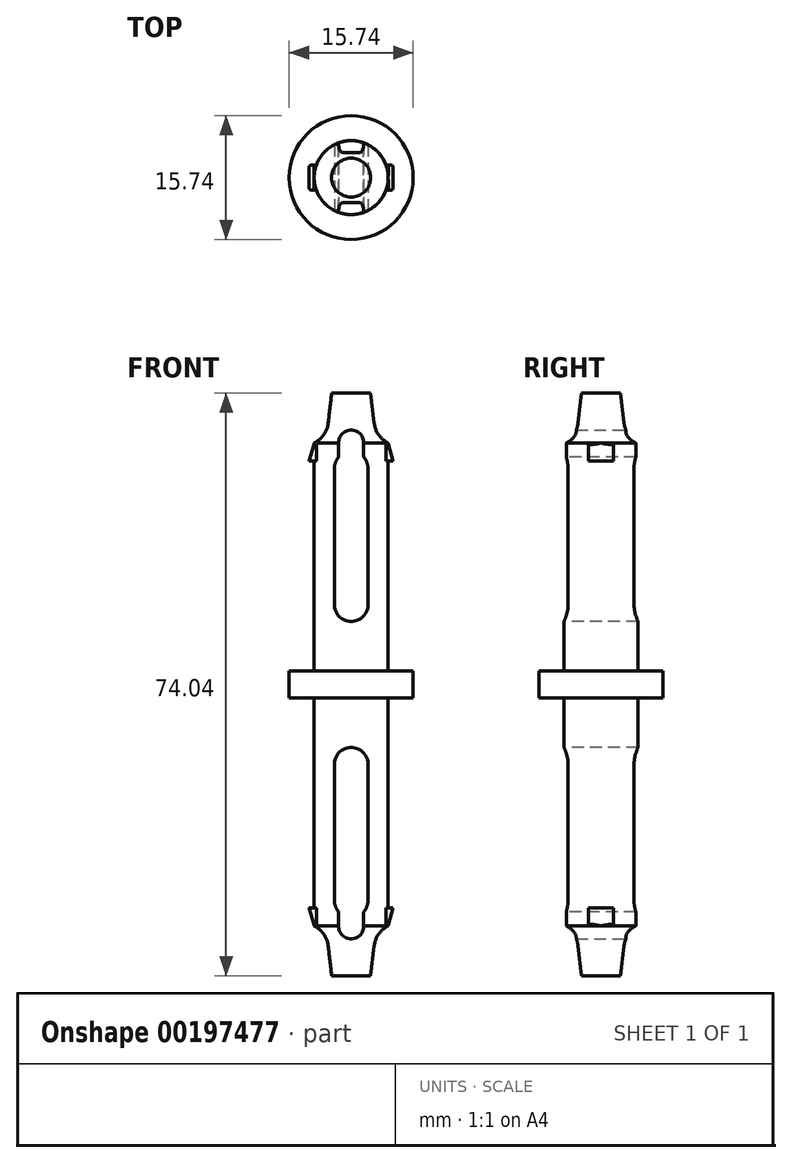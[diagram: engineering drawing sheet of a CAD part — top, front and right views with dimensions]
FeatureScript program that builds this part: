
annotation { "Feature Type Name" : "Feature", "Feature Type Description" : "" }
export const myFeature = defineFeature(function(context is Context, id is Id, definition is map)
    precondition{}
    {
        {
            var Q0;
            Q0=qCreatedBy(makeId("Top.planeOp"),FACE);
            var sketch = newSketch(context, id + "F0", { "sketchPlane" : qUnion([Q0])});
            skCircle(sketch, "E0", {"center": v(0, 0) * mm, "radius": 7.87 * mm});
            skSolve(sketch);
        }
        {
            var Q0;
            Q0=makeQuery(id+"F0.imprint","IMPRINT",FACE,{"disambiguationData":[TD([[makeQuery(id+"F0.imprint","IMPRINT",EDGE,{"derivedFrom":sQuery(id+"F0.wireOp",EDGE,"E0")}),1.0]])]});
            extrude(context, id + "F1", {"entities" : qUnion([Q0]), "endBound" : BoundingType.SYMMETRIC, "depth" : 3.43 * mm});
        }
        {
            var Q0;
            Q0=qCreatedBy(makeId("Front.planeOp"),FACE);
            var sketch = newSketch(context, id + "F2", { "sketchPlane" : qUnion([Q0])});
            skLineSegment(sketch, "E1", {"start": v(0, 1.71) * mm, "end": v(0, 37.02) * mm});
            skLineSegment(sketch, "E2", {"start": v(0, 1.71) * mm, "end": v(-4.7, 1.71) * mm});
            skLineSegment(sketch, "E3", {"start": v(-4.7, 1.71) * mm, "end": v(-4.7, 30.67) * mm});
            skLineSegment(sketch, "E4", {"start": v(0, 37.02) * mm, "end": v(-2.48, 37.02) * mm});
            skLineSegment(sketch, "E5", {"start": v(-2.48, 37.02) * mm, "end": v(-2.92, 33.21) * mm});
            skArc(sketch, "E6", {"start": v(-2.92, 33.21) * mm, "mid": v(-3.49, 31.72) * mm, "end": v(-4.7, 30.67) * mm});
            skSolve(sketch);
        }
        {
            var Q0;
            Q0 = qSketchRegion(id + "F2", true);
            var Q1;
            Q1=sQuery(id+"F2.wireOp",EDGE,"E1");
            revolve(context, id + "F3", {"operationType" : NewBodyOperationType.ADD, "entities" : qUnion([Q0]), "axis" : qUnion([Q1]), "revolveType" : RevolveType.FULL});
        }
        {
            var Q0;
            Q0=qCreatedBy(makeId("Front.planeOp"),FACE);
            var sketch = newSketch(context, id + "F4", { "sketchPlane" : qUnion([Q0])});
            skLineSegment(sketch, "E7", {"start": v(0, 10.13) * mm, "end": v(0, 27.48) * mm});
            skArc(sketch, "E8.0.startCap", {"start": v(2.13, 10.13) * mm, "mid": v(0, 8) * mm, "end": v(-2.13, 10.13) * mm});
            skArc(sketch, "E8.0.endCap", {"start": v(-2.13, 27.48) * mm, "mid": v(0, 29.6) * mm, "end": v(2.13, 27.48) * mm});
            skLineSegment(sketch, "E8.0.left", {"start": v(-2.13, 10.13) * mm, "end": v(-2.13, 27.48) * mm});
            skLineSegment(sketch, "E8.0.right", {"start": v(2.13, 10.13) * mm, "end": v(2.13, 27.48) * mm});
            skLineSegment(sketch, "E9", {"start": v(-4.7, 28.9) * mm, "end": v(-1.59, 28.9) * mm, "construction": true});
            skLineSegment(sketch, "E10", {"start": v(-4.7, 30.67) * mm, "end": v(-4.7, 28.9) * mm, "construction": true});
            skSolve(sketch);
        }
        {
            var Q0;
            Q0 = qSketchRegion(id + "F4", true);
            extrude(context, id + "F5", {"entities" : qUnion([Q0]), "operationType" : NewBodyOperationType.REMOVE, "endBound" : BoundingType.SYMMETRIC, "oppositeDirection" : true, "depth" : 25.4 * mm});
        }
        {
            var Q0;
            Q0=qCreatedBy(makeId("Front.planeOp"),FACE);
            var sketch = newSketch(context, id + "F6", { "sketchPlane" : qUnion([Q0])});
            skLineSegment(sketch, "E11", {"start": v(0, 25.4) * mm, "end": v(0, 30.73) * mm, "construction": true});
            skArc(sketch, "E12.0.startCap", {"start": v(1.59, 25.4) * mm, "mid": v(0, 23.81) * mm, "end": v(-1.59, 25.4) * mm});
            skArc(sketch, "E12.0.endCap", {"start": v(-1.59, 30.73) * mm, "mid": v(0, 32.32) * mm, "end": v(1.59, 30.73) * mm});
            skLineSegment(sketch, "E12.0.left", {"start": v(-1.59, 25.4) * mm, "end": v(-1.59, 30.73) * mm});
            skLineSegment(sketch, "E12.0.right", {"start": v(1.59, 25.4) * mm, "end": v(1.59, 30.73) * mm});
            skSolve(sketch);
        }
        {
            var Q0;
            Q0 = qSketchRegion(id + "F6", true);
            extrude(context, id + "F7", {"entities" : qUnion([Q0]), "operationType" : NewBodyOperationType.REMOVE, "endBound" : BoundingType.SYMMETRIC, "depth" : 25.4 * mm});
        }
        {
            var Q0;
            Q0=qCreatedBy(makeId("Front.planeOp"),FACE);
            var sketch = newSketch(context, id + "F8", { "sketchPlane" : qUnion([Q0])});
            skLineSegment(sketch, "E13", {"start": v(3.11, 28.38) * mm, "end": v(5.33, 28.38) * mm});
            skLineSegment(sketch, "E14", {"start": v(5.33, 28.38) * mm, "end": v(4.7, 30.67) * mm});
            skLineSegment(sketch, "E15", {"start": v(4.7, 30.67) * mm, "end": v(3.11, 30.67) * mm});
            skLineSegment(sketch, "E16", {"start": v(3.11, 30.67) * mm, "end": v(3.11, 28.38) * mm});
            skSolve(sketch);
        }
        {
            var Q0;
            Q0 = qSketchRegion(id + "F8", true);
            extrude(context, id + "F9", {"entities" : qUnion([Q0]), "operationType" : NewBodyOperationType.ADD, "endBound" : BoundingType.SYMMETRIC, "depth" : 3.17 * mm});
        }
        {
            var Q0;
            Q0=makeQuery(id+"F1.opExtrude","SWEPT_BODY",BODY,{"disambiguationData":[OSD([sQuery(id+"F0.wireOp",EDGE,"E0")])]});
            var Q1;
            Q1=qCreatedBy(makeId("Right.planeOp"),FACE);
            mirror(context, id + "F10", {"operationType" : NewBodyOperationType.ADD, "entities" : qUnion([Q0]), "mirrorPlane" : qUnion([Q1])});
        }
        {
            var Q0;
            {var subQ0=sQuery(id+"F8.wireOp",EDGE,"E15");var subQ1=sQuery(id+"F8.wireOp",EDGE,"E14");Q0=makeQuery(id+"F10.opPattern","COPY",EDGE,{"derivedFrom":makeQuery(id+"F9.boolean.opBoolean","SPLIT",EDGE,{"disambiguationData":[TD([makeQuery(id+"F9.opExtrude","CAP_FACE",FACE,{"disambiguationData":[OSD([sQuery(id+"F8.wireOp",EDGE,"E13"),subQ1,subQ0,sQuery(id+"F8.wireOp",EDGE,"E16")])],"isStart":false})])],"derivedFrom":makeQuery(id+"F9.opExtrude","SWEPT_EDGE",EDGE,{"disambiguationData":[OSD([subQ1,subQ0])]})}),"instanceName":"1"});}
            var Q1;
            {var subQ0=sQuery(id+"F8.wireOp",EDGE,"E15");var subQ1=sQuery(id+"F8.wireOp",EDGE,"E14");Q1=makeQuery(id+"F9.boolean.opBoolean","SPLIT",EDGE,{"disambiguationData":[TD([makeQuery(id+"F9.opExtrude","CAP_FACE",FACE,{"disambiguationData":[OSD([sQuery(id+"F8.wireOp",EDGE,"E13"),subQ1,subQ0,sQuery(id+"F8.wireOp",EDGE,"E16")])],"isStart":false})])],"derivedFrom":makeQuery(id+"F9.opExtrude","SWEPT_EDGE",EDGE,{"disambiguationData":[OSD([subQ1,subQ0])]})});}
            var Q2;
            Q2=makeQuery(id+"F10.opPattern","COPY",EDGE,{"derivedFrom":makeQuery(id+"F9.opExtrude","CAP_EDGE",EDGE,{"disambiguationData":[OSD([sQuery(id+"F8.wireOp",EDGE,"E15")])],"isStart":false}),"instanceName":"1"});
            var Q3;
            Q3=makeQuery(id+"F10.opPattern","COPY",EDGE,{"derivedFrom":makeQuery(id+"F9.opExtrude","CAP_EDGE",EDGE,{"disambiguationData":[OSD([sQuery(id+"F8.wireOp",EDGE,"E14")])],"isStart":false}),"instanceName":"1"});
            var Q4;
            Q4=makeQuery(id+"F10.opPattern","COPY",EDGE,{"derivedFrom":makeQuery(id+"F9.opExtrude","CAP_EDGE",EDGE,{"disambiguationData":[OSD([sQuery(id+"F8.wireOp",EDGE,"E14")])],"isStart":true}),"instanceName":"1"});
            var Q5;
            Q5=makeQuery(id+"F10.opPattern","COPY",EDGE,{"derivedFrom":makeQuery(id+"F9.opExtrude","CAP_EDGE",EDGE,{"disambiguationData":[OSD([sQuery(id+"F8.wireOp",EDGE,"E15")])],"isStart":true}),"instanceName":"1"});
            var Q6;
            Q6=makeQuery(id+"F9.opExtrude","CAP_EDGE",EDGE,{"disambiguationData":[OSD([sQuery(id+"F8.wireOp",EDGE,"E14")])],"isStart":false});
            var Q7;
            Q7=makeQuery(id+"F9.opExtrude","CAP_EDGE",EDGE,{"disambiguationData":[OSD([sQuery(id+"F8.wireOp",EDGE,"E15")])],"isStart":false});
            var Q8;
            Q8=makeQuery(id+"F9.opExtrude","CAP_EDGE",EDGE,{"disambiguationData":[OSD([sQuery(id+"F8.wireOp",EDGE,"E15")])],"isStart":true});
            var Q9;
            Q9=makeQuery(id+"F9.opExtrude","CAP_EDGE",EDGE,{"disambiguationData":[OSD([sQuery(id+"F8.wireOp",EDGE,"E14")])],"isStart":true});
            fillet(context, id + "F11", {"entities" : qUnion([Q0, Q1, Q2, Q3, Q4, Q5, Q6, Q7, Q8, Q9]), "radius" : 0.25 * mm, "tangentPropagation" : true, "allowEdgeOverflow" : false});
        }
        {
            var Q0;
            Q0=makeQuery(id+"F1.opExtrude","SWEPT_BODY",BODY,{"disambiguationData":[OSD([sQuery(id+"F0.wireOp",EDGE,"E0")])]});
            var Q1;
            Q1=qCreatedBy(makeId("Top.planeOp"),FACE);
            mirror(context, id + "F12", {"operationType" : NewBodyOperationType.ADD, "entities" : qUnion([Q0]), "mirrorPlane" : qUnion([Q1])});
        }
    });
